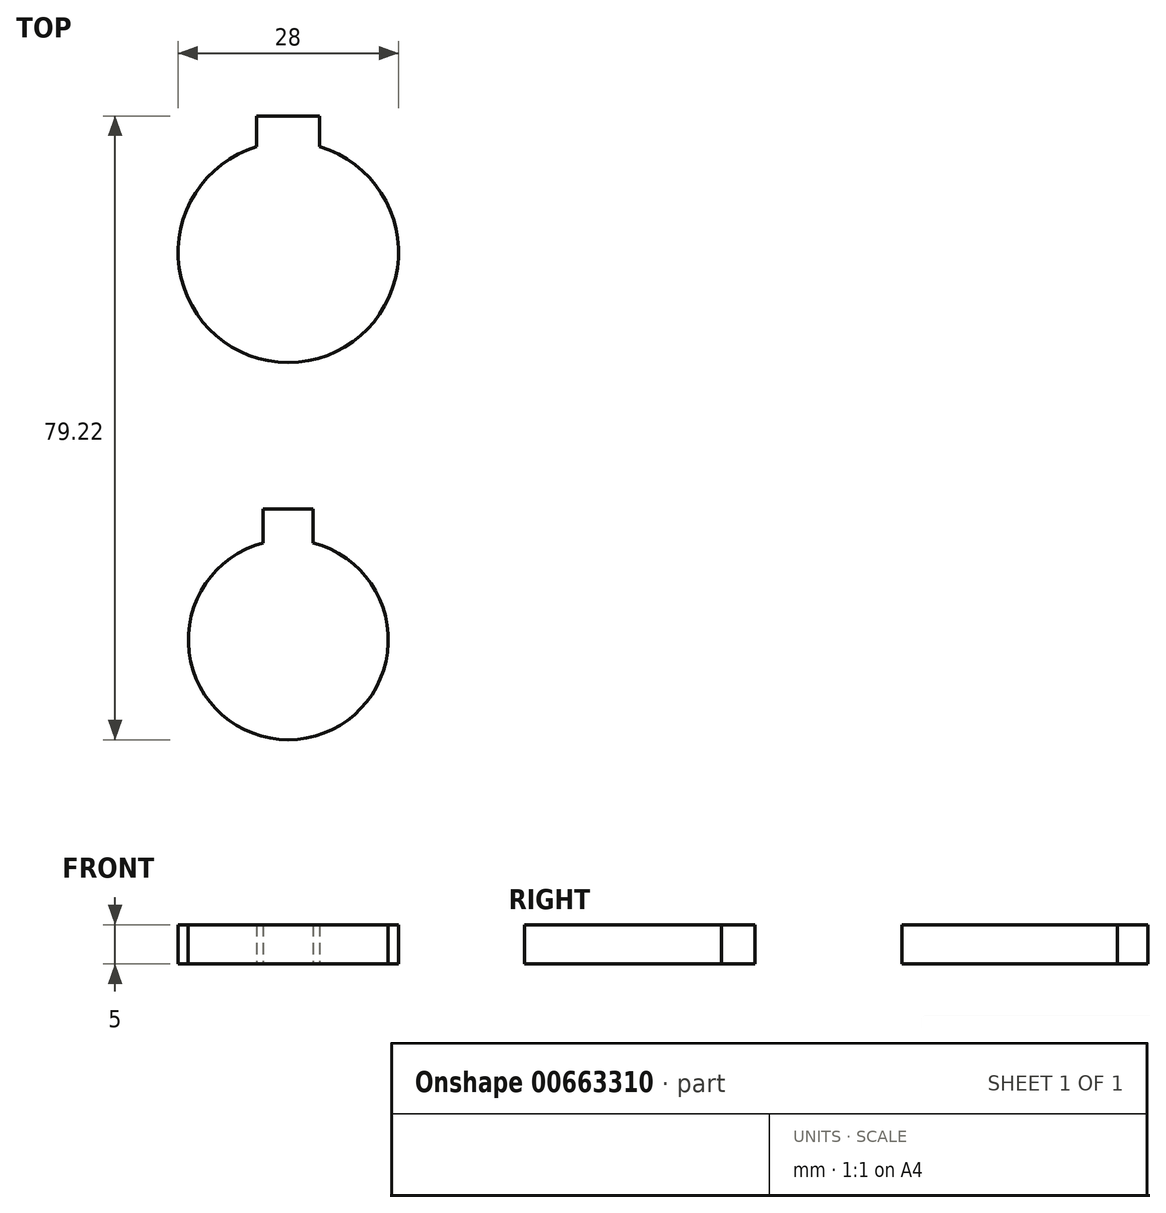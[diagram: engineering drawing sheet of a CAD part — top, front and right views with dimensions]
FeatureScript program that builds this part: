
annotation { "Feature Type Name" : "Feature", "Feature Type Description" : "" }
export const myFeature = defineFeature(function(context is Context, id is Id, definition is map)
    precondition{}
    {
        {
            var Q0;
            Q0=qCreatedBy(makeId("Top.planeOp"),FACE);
            var sketch = newSketch(context, id + "F0", { "sketchPlane" : qUnion([Q0])});
            skArc(sketch, "E0", {"start": v(-4, 13.42) * mm, "mid": v(0, -14) * mm, "end": v(4, 13.42) * mm});
            skLineSegment(sketch, "E1.bottom", {"start": v(-4, 17.3) * mm, "end": v(4, 17.3) * mm});
            skLineSegment(sketch, "E1.left", {"start": v(-4, 17.3) * mm, "end": v(-4, 13.42) * mm});
            skLineSegment(sketch, "E1.right", {"start": v(4, 17.3) * mm, "end": v(4, 13.42) * mm});
            skLineSegment(sketch, "E2", {"start": v(0, 17.3) * mm, "end": v(0, -14) * mm, "construction": true});
            skArc(sketch, "E3", {"start": v(-3.18, -36.92) * mm, "mid": v(0, -61.92) * mm, "end": v(3.18, -36.92) * mm});
            skLineSegment(sketch, "E4.bottom", {"start": v(-3.17, -32.62) * mm, "end": v(3.18, -32.62) * mm});
            skLineSegment(sketch, "E4.left", {"start": v(-3.17, -32.62) * mm, "end": v(-3.17, -36.92) * mm});
            skLineSegment(sketch, "E4.right", {"start": v(3.18, -32.62) * mm, "end": v(3.18, -36.92) * mm});
            skLineSegment(sketch, "E5", {"start": v(0, -32.62) * mm, "end": v(0, -61.92) * mm, "construction": true});
            skSolve(sketch);
        }
        {
            var Q0;
            Q0 = qSketchRegion(id + "F0", true);
            extrude(context, id + "F1", {"entities" : qUnion([Q0]), "depth" : 5 * mm, "offsetDistance" : 25 * mm});
        }
    });
